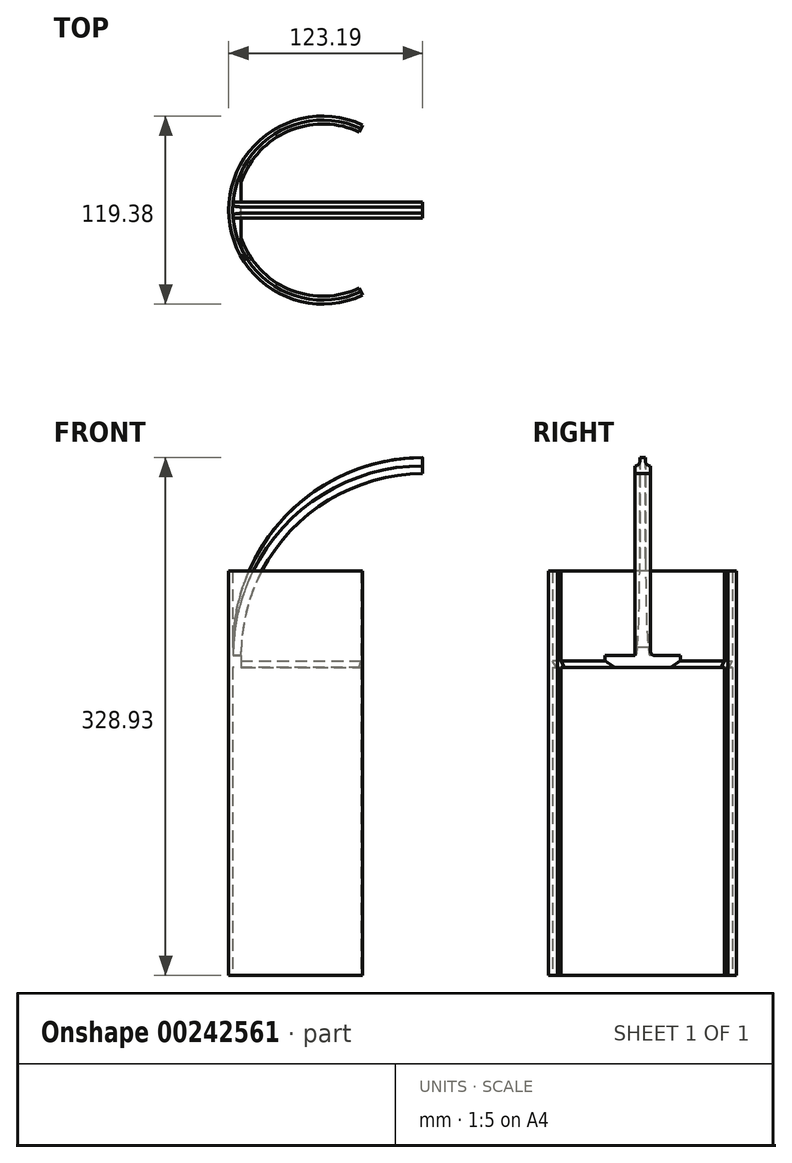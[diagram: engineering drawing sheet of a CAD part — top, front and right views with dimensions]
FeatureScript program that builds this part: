
annotation { "Feature Type Name" : "Feature", "Feature Type Description" : "" }
export const myFeature = defineFeature(function(context is Context, id is Id, definition is map)
    precondition{}
    {
        {
            var Q0;
            Q0=qCreatedBy(makeId("Top.planeOp"),FACE);
            var sketch = newSketch(context, id + "F0", { "sketchPlane" : qUnion([Q0])});
            skLineSegment(sketch, "E0.bottom", {"start": v(0, 5) * mm, "end": v(-31.75, 5) * mm});
            skLineSegment(sketch, "E0.top", {"start": v(0, -5) * mm, "end": v(-31.75, -5) * mm});
            skLineSegment(sketch, "E0.left", {"start": v(0, 5) * mm, "end": v(0, -5) * mm});
            skLineSegment(sketch, "E0.right", {"start": v(-31.75, 5) * mm, "end": v(-31.75, -5) * mm});
            skCircle(sketch, "E1", {"center": v(-63.5, 0) * mm, "radius": 57.15 * mm});
            skLineSegment(sketch, "E2", {"start": v(-63.5, 0) * mm, "end": v(-39.35, 51.8) * mm});
            skLineSegment(sketch, "E3", {"start": v(-63.5, 0) * mm, "end": v(-39.35, -51.8) * mm});
            skCircle(sketch, "E4", {"center": v(-63.5, 0) * mm, "radius": 49.65 * mm});
            skLineSegment(sketch, "E5.bottom", {"start": v(-120.43, -5) * mm, "end": v(-94.98, -5) * mm});
            skLineSegment(sketch, "E5.top", {"start": v(-120.43, 5) * mm, "end": v(-94.98, 5) * mm});
            skLineSegment(sketch, "E5.left", {"start": v(-120.43, -5) * mm, "end": v(-120.43, 5) * mm});
            skLineSegment(sketch, "E5.right", {"start": v(-94.98, -5) * mm, "end": v(-94.98, 5) * mm});
            skPoint(sketch, "E5.middle", {"position": v(-107.7, 0) * mm});
            skLineSegment(sketch, "E6.bottom", {"start": v(-112.9, -5) * mm, "end": v(-115.44, -5) * mm});
            skLineSegment(sketch, "E6.top", {"start": v(-112.9, 5) * mm, "end": v(-115.44, 5) * mm});
            skLineSegment(sketch, "E6.left", {"start": v(-112.9, -5) * mm, "end": v(-112.9, 5) * mm});
            skLineSegment(sketch, "E6.right", {"start": v(-115.44, -5) * mm, "end": v(-115.44, 5) * mm});
            skLineSegment(sketch, "E7", {"start": v(-115.44, -5) * mm, "end": v(-109.06, -19.72) * mm});
            skLineSegment(sketch, "E8", {"start": v(-115.44, 5) * mm, "end": v(-109.06, 19.72) * mm});
            skSolve(sketch);
        }
        {
            var Q0;
            {var subQ0=sQuery(id+"F0.wireOp",EDGE,"E5.left");Q0=makeQuery(id+"F0.imprint","IMPRINT",FACE,{"disambiguationData":[TD([[makeQuery(id+"F0.imprint","IMPRINT",EDGE,{"derivedFrom":subQ0}),1.0]])]});}
            var Q1;
            {var subQ0=sQuery(id+"F0.wireOp",EDGE,"E2");var subQ1=sQuery(id+"F0.wireOp",EDGE,"E1");var subQ2=makeQuery(id+"F0.imprint","INTERSECT",VERTEX,{"derivedFrom":[subQ1,subQ0]});Q1=makeQuery(id+"F0.imprint","IMPRINT",FACE,{"disambiguationData":[TD([[makeQuery(id+"F0.imprint","IMPRINT",EDGE,{"disambiguationData":[TD([[subQ2,1.0]])],"derivedFrom":subQ0}),1.0]])]});}
            var Q2;
            {var subQ0=sQuery(id+"F0.wireOp",EDGE,"E3");var subQ1=sQuery(id+"F0.wireOp",EDGE,"E1");var subQ2=makeQuery(id+"F0.imprint","INTERSECT",VERTEX,{"derivedFrom":[subQ1,subQ0]});Q2=makeQuery(id+"F0.imprint","IMPRINT",FACE,{"disambiguationData":[TD([[makeQuery(id+"F0.imprint","IMPRINT",EDGE,{"disambiguationData":[TD([[subQ2,1.0]])],"derivedFrom":subQ0}),-1.0]])]});}
            var Q3;
            {var subQ5=sQuery(id+"F0.wireOp",EDGE,"E5.left");Q3=makeQuery(id+"F0.imprint","IMPRINT",FACE,{"disambiguationData":[TD([[makeQuery(id+"F0.imprint","IMPRINT",EDGE,{"derivedFrom":subQ5}),-1.0]])]});}
            extrude(context, id + "F1", {"entities" : qUnion([Q0, Q1, Q2, Q3]), "oppositeDirection" : true, "depth" : 7.62 * mm});
        }
        {
            var Q0;
            {var subQ5=sQuery(id+"F0.wireOp",EDGE,"E5.left");Q0=makeQuery(id+"F0.imprint","IMPRINT",FACE,{"disambiguationData":[TD([[makeQuery(id+"F0.imprint","IMPRINT",EDGE,{"derivedFrom":subQ5}),-1.0]])]});}
            var Q1;
            {var subQ0=sQuery(id+"F0.wireOp",EDGE,"E5.left");Q1=makeQuery(id+"F0.imprint","IMPRINT",FACE,{"disambiguationData":[TD([[makeQuery(id+"F0.imprint","IMPRINT",EDGE,{"derivedFrom":subQ0}),1.0]])]});}
            var Q2;
            Q2=sQuery(id+"F0.wireOp",EDGE,"E0.left");
            revolve(context, id + "F2", {"operationType" : NewBodyOperationType.ADD, "entities" : qUnion([Q0, Q1]), "axis" : qUnion([Q2]), "revolveType" : RevolveType.ONE_DIRECTION, "oppositeDirection" : true, "angle" : 90 * degree});
        }
        {
            var Q0;
            Q0=makeQuery(id+"F1.opExtrude","CAP_EDGE",EDGE,{"disambiguationData":[OSD([sQuery(id+"F0.wireOp",EDGE,"E4")])],"isStart":false});
            chamfer(context, id + "F3", {"entities" : qUnion([Q0]), "chamferType" : ChamferType.OFFSET_ANGLE, "width" : 5.08 * mm, "oppositeDirection" : false, "angle" : 61 * degree, "tangentPropagation" : true});
        }
        {
            var Q0;
            Q0=qCreatedBy(makeId("Top.planeOp"),FACE);
            var sketch = newSketch(context, id + "F4", { "sketchPlane" : qUnion([Q0])});
            skArc(sketch, "E9.0", {"start": v(-122.96, -5.22) * mm, "mid": v(-93.34, -51.7) * mm, "end": v(-38.27, -54.1) * mm});
            skArc(sketch, "E9.1", {"start": v(-122.96, 5.22) * mm, "mid": v(-123.2, 0) * mm, "end": v(-122.96, -5.22) * mm});
            skArc(sketch, "E9.2", {"start": v(-38.27, 54.1) * mm, "mid": v(-93.34, 51.7) * mm, "end": v(-122.96, 5.22) * mm});
            skArc(sketch, "E10.0", {"start": v(-39.35, 51.8) * mm, "mid": v(-92.07, 49.5) * mm, "end": v(-120.43, 5) * mm});
            skArc(sketch, "E11.0", {"start": v(-120.43, 5) * mm, "mid": v(-120.65, 0) * mm, "end": v(-120.43, -5) * mm});
            skArc(sketch, "E12.0", {"start": v(-120.43, -5) * mm, "mid": v(-92.07, -49.5) * mm, "end": v(-39.35, -51.8) * mm});
            skLineSegment(sketch, "E13", {"start": v(-39.35, 51.8) * mm, "end": v(-38.27, 54.1) * mm});
            skLineSegment(sketch, "E14", {"start": v(-39.35, -51.8) * mm, "end": v(-38.27, -54.1) * mm});
            skSolve(sketch);
        }
        {
            var Q0;
            Q0 = qSketchRegion(id + "F4", true);
            extrude(context, id + "F5", {"entities" : qUnion([Q0]), "depth" : 53.6 * mm});
        }
        {
            var Q0;
            Q0=makeQuery(id+"F5.opExtrude","CAP_FACE",FACE,{"disambiguationData":[OSD([sQuery(id+"F4.wireOp",EDGE,"E9.0"),sQuery(id+"F4.wireOp",EDGE,"E9.1"),sQuery(id+"F4.wireOp",EDGE,"E9.2"),sQuery(id+"F4.wireOp",EDGE,"E10.0"),sQuery(id+"F4.wireOp",EDGE,"E11.0"),sQuery(id+"F4.wireOp",EDGE,"E12.0"),sQuery(id+"F4.wireOp",EDGE,"E13"),sQuery(id+"F4.wireOp",EDGE,"E14")])],"isStart":true});
            extrude(context, id + "F6", {"entities" : qUnion([Q0]), "operationType" : NewBodyOperationType.ADD, "depth" : 203.2 * mm});
        }
        {
            var Q0;
            {var subQ0=sQuery(id+"F0.wireOp",EDGE,"E6.right");var subQ1=sQuery(id+"F0.wireOp",EDGE,"E2");var subQ2=sQuery(id+"F0.wireOp",EDGE,"E8");var subQ3=sQuery(id+"F0.wireOp",EDGE,"E4");var subQ4=makeQuery(id+"F0.imprint","IMPRINT",EDGE,{"disambiguationData":[TD([[makeQuery(id+"F0.imprint","INTERSECT",VERTEX,{"derivedFrom":[subQ3,subQ2]}),1.0]])],"derivedFrom":subQ3});var subQ5=sQuery(id+"F0.wireOp",EDGE,"E1");Q0=makeQuery(id+"F3.opChamfer","BLEND_EDGE",EDGE,{"blendedFrom":[makeQuery(id+"F1.opExtrude","CAP_EDGE",EDGE,{"disambiguationData":[OSD([subQ3]),TDD([subQ4])],"isStart":false}),makeQuery(id+"F2.boolean.opBoolean","SPLIT",FACE,{"disambiguationData":[TD([makeQuery(id+"F1.opExtrude","SWEPT_FACE",FACE,{"disambiguationData":[OSD([subQ1])]})])],"derivedFrom":makeQuery(id+"F1.opExtrude","CAP_FACE",FACE,{"disambiguationData":[OSD([subQ5,subQ1,sQuery(id+"F0.wireOp",EDGE,"E3"),subQ3,subQ0,sQuery(id+"F0.wireOp",EDGE,"E7"),subQ2])],"isStart":true})})],"blendedInto":[makeQuery(id+"F2.boolean.opBoolean","SPLIT",FACE,{"disambiguationData":[TD([makeQuery(id+"F1.opExtrude","SWEPT_FACE",FACE,{"disambiguationData":[OSD([subQ1])]})])],"derivedFrom":makeQuery(id+"F1.opExtrude","CAP_FACE",FACE,{"disambiguationData":[OSD([subQ5,subQ1,sQuery(id+"F0.wireOp",EDGE,"E3"),subQ3,subQ0,sQuery(id+"F0.wireOp",EDGE,"E7"),subQ2])],"isStart":true})})]});}
            var Q1;
            {var subQ0=sQuery(id+"F0.wireOp",EDGE,"E6.right");var subQ1=sQuery(id+"F0.wireOp",EDGE,"E7");var subQ2=sQuery(id+"F0.wireOp",EDGE,"E4");var subQ3=sQuery(id+"F0.wireOp",EDGE,"E3");var subQ4=makeQuery(id+"F0.imprint","IMPRINT",EDGE,{"disambiguationData":[TD([[makeQuery(id+"F0.imprint","INTERSECT",VERTEX,{"derivedFrom":[subQ2,subQ1]}),-1.0]])],"derivedFrom":subQ2});var subQ5=sQuery(id+"F0.wireOp",EDGE,"E1");Q1=makeQuery(id+"F3.opChamfer","BLEND_EDGE",EDGE,{"blendedFrom":[makeQuery(id+"F1.opExtrude","CAP_EDGE",EDGE,{"disambiguationData":[OSD([subQ2]),TDD([subQ4])],"isStart":false}),makeQuery(id+"F2.boolean.opBoolean","SPLIT",FACE,{"disambiguationData":[TD([makeQuery(id+"F1.opExtrude","SWEPT_FACE",FACE,{"disambiguationData":[OSD([subQ3])]})])],"derivedFrom":makeQuery(id+"F1.opExtrude","CAP_FACE",FACE,{"disambiguationData":[OSD([subQ5,sQuery(id+"F0.wireOp",EDGE,"E2"),subQ3,subQ2,subQ0,subQ1,sQuery(id+"F0.wireOp",EDGE,"E8")])],"isStart":true})})],"blendedInto":[makeQuery(id+"F2.boolean.opBoolean","SPLIT",FACE,{"disambiguationData":[TD([makeQuery(id+"F1.opExtrude","SWEPT_FACE",FACE,{"disambiguationData":[OSD([subQ3])]})])],"derivedFrom":makeQuery(id+"F1.opExtrude","CAP_FACE",FACE,{"disambiguationData":[OSD([subQ5,sQuery(id+"F0.wireOp",EDGE,"E2"),subQ3,subQ2,subQ0,subQ1,sQuery(id+"F0.wireOp",EDGE,"E8")])],"isStart":true})})]});}
            var Q2;
            {var subQ0=sQuery(id+"F0.wireOp",EDGE,"E6.right");var subQ1=sQuery(id+"F0.wireOp",EDGE,"E7");var subQ2=sQuery(id+"F0.wireOp",EDGE,"E4");var subQ3=sQuery(id+"F0.wireOp",EDGE,"E3");var subQ4=sQuery(id+"F0.wireOp",EDGE,"E1");Q2=makeQuery(id+"F3.opChamfer","BLEND_EDGE",EDGE,{"blendedFrom":[makeQuery(id+"F1.opExtrude","CAP_EDGE",EDGE,{"disambiguationData":[OSD([subQ1])],"isStart":false}),makeQuery(id+"F2.boolean.opBoolean","SPLIT",FACE,{"disambiguationData":[TD([makeQuery(id+"F1.opExtrude","SWEPT_FACE",FACE,{"disambiguationData":[OSD([subQ3])]})])],"derivedFrom":makeQuery(id+"F1.opExtrude","CAP_FACE",FACE,{"disambiguationData":[OSD([subQ4,sQuery(id+"F0.wireOp",EDGE,"E2"),subQ3,subQ2,subQ0,subQ1,sQuery(id+"F0.wireOp",EDGE,"E8")])],"isStart":true})})],"blendedInto":[makeQuery(id+"F2.boolean.opBoolean","SPLIT",FACE,{"disambiguationData":[TD([makeQuery(id+"F1.opExtrude","SWEPT_FACE",FACE,{"disambiguationData":[OSD([subQ3])]})])],"derivedFrom":makeQuery(id+"F1.opExtrude","CAP_FACE",FACE,{"disambiguationData":[OSD([subQ4,sQuery(id+"F0.wireOp",EDGE,"E2"),subQ3,subQ2,subQ0,subQ1,sQuery(id+"F0.wireOp",EDGE,"E8")])],"isStart":true})})]});}
            var Q3;
            {var subQ0=sQuery(id+"F0.wireOp",EDGE,"E6.right");var subQ1=sQuery(id+"F0.wireOp",EDGE,"E2");var subQ2=sQuery(id+"F0.wireOp",EDGE,"E8");var subQ3=sQuery(id+"F0.wireOp",EDGE,"E4");var subQ4=sQuery(id+"F0.wireOp",EDGE,"E1");Q3=makeQuery(id+"F3.opChamfer","BLEND_EDGE",EDGE,{"blendedFrom":[makeQuery(id+"F1.opExtrude","CAP_EDGE",EDGE,{"disambiguationData":[OSD([subQ2])],"isStart":false}),makeQuery(id+"F2.boolean.opBoolean","SPLIT",FACE,{"disambiguationData":[TD([makeQuery(id+"F1.opExtrude","SWEPT_FACE",FACE,{"disambiguationData":[OSD([subQ1])]})])],"derivedFrom":makeQuery(id+"F1.opExtrude","CAP_FACE",FACE,{"disambiguationData":[OSD([subQ4,subQ1,sQuery(id+"F0.wireOp",EDGE,"E3"),subQ3,subQ0,sQuery(id+"F0.wireOp",EDGE,"E7"),subQ2])],"isStart":true})})],"blendedInto":[makeQuery(id+"F2.boolean.opBoolean","SPLIT",FACE,{"disambiguationData":[TD([makeQuery(id+"F1.opExtrude","SWEPT_FACE",FACE,{"disambiguationData":[OSD([subQ1])]})])],"derivedFrom":makeQuery(id+"F1.opExtrude","CAP_FACE",FACE,{"disambiguationData":[OSD([subQ4,subQ1,sQuery(id+"F0.wireOp",EDGE,"E3"),subQ3,subQ0,sQuery(id+"F0.wireOp",EDGE,"E7"),subQ2])],"isStart":true})})]});}
            chamfer(context, id + "F7", {"entities" : qUnion([Q0, Q1, Q2, Q3]), "width" : 5.08 * mm, "tangentPropagation" : true});
        }
        {
            var Q0;
            Q0=qCreatedBy(makeId("Top.planeOp"),FACE);
            var sketch = newSketch(context, id + "F8", { "sketchPlane" : qUnion([Q0])});
            skLineSegment(sketch, "E15.bottom", {"start": v(-120.62, -1.86) * mm, "end": v(-115.44, -1.86) * mm});
            skLineSegment(sketch, "E15.top", {"start": v(-120.62, 1.86) * mm, "end": v(-115.44, 1.86) * mm});
            skLineSegment(sketch, "E15.left", {"start": v(-120.62, -1.86) * mm, "end": v(-120.62, 1.86) * mm});
            skLineSegment(sketch, "E15.right", {"start": v(-115.44, -1.86) * mm, "end": v(-115.44, 1.86) * mm});
            skPoint(sketch, "E15.middle", {"position": v(-118.03, 0) * mm});
            skCircle(sketch, "E16.0", {"center": v(-63.5, 0) * mm, "radius": 57.15 * mm});
            skCircle(sketch, "E17.0", {"center": v(-63.5, 0) * mm, "radius": 49.65 * mm});
            skLineSegment(sketch, "E18.0", {"start": v(-115.44, -5) * mm, "end": v(-115.44, 5) * mm});
            skSolve(sketch);
        }
        {
            var Q0;
            {var subQ0=sQuery(id+"F8.wireOp",EDGE,"E15.bottom");Q0=makeQuery(id+"F8.imprint","IMPRINT",FACE,{"disambiguationData":[TD([[makeQuery(id+"F8.imprint","IMPRINT",EDGE,{"derivedFrom":subQ0}),1.0]])]});}
            var Q1;
            {var subQ0=sQuery(id+"F8.wireOp",EDGE,"E15.left");Q1=makeQuery(id+"F8.imprint","IMPRINT",FACE,{"disambiguationData":[TD([[makeQuery(id+"F8.imprint","IMPRINT",EDGE,{"derivedFrom":subQ0}),1.0]])]});}
            var Q2;
            Q2=sQuery(id+"F0.wireOp",EDGE,"E0.left");
            revolve(context, id + "F9", {"entities" : qUnion([Q0, Q1]), "axis" : qUnion([Q2]), "revolveType" : RevolveType.ONE_DIRECTION, "oppositeDirection" : true, "angle" : 90 * degree});
        }
        {
            var Q0;
            Q0=makeQuery(id+"F9.opRevolve","SWEPT_BODY",BODY,{"disambiguationData":[OSD([sQuery(id+"F8.wireOp",EDGE,"E15.bottom"),sQuery(id+"F8.wireOp",EDGE,"E15.top"),sQuery(id+"F8.wireOp",EDGE,"E16.0"),sQuery(id+"F8.wireOp",EDGE,"E18.0")])]});
            var Q1;
            {var subQ0=sQuery(id+"F4.wireOp",EDGE,"E14");var subQ1=sQuery(id+"F4.wireOp",EDGE,"E9.0");Q1=makeQuery(id+"F6.boolean.opBoolean","MERGE",EDGE,{"derivedFrom":[makeQuery(id+"F5.opExtrude","SWEPT_EDGE",EDGE,{"disambiguationData":[OSD([subQ1,subQ0])]}),makeQuery(id+"F6.opExtrude","SWEPT_EDGE",EDGE,{"disambiguationData":[OSD([subQ1,subQ0])]})]});}
            transform(context, id + "F10", {"entities" : qUnion([Q0]), "transformType" : TransformType.TRANSLATION_3D, "dx" : 0 * mm, "dy" : 0 * mm, "dz" : 5.08 * mm, "makeCopy" : false});
        }
        {
            var Q0;
            Q0=makeQuery(id+"F9.opRevolve","CAP_FACE",FACE,{"disambiguationData":[OSD([sQuery(id+"F8.wireOp",EDGE,"E15.bottom"),sQuery(id+"F8.wireOp",EDGE,"E15.top"),sQuery(id+"F8.wireOp",EDGE,"E16.0"),sQuery(id+"F8.wireOp",EDGE,"E18.0")])],"isStart":true});
            extrude(context, id + "F11", {"entities" : qUnion([Q0]), "operationType" : NewBodyOperationType.ADD, "depth" : 10.26 * mm});
        }
        {
            var Q0;
            Q0=makeQuery(id+"F2.opRevolve","CAP_EDGE",EDGE,{"disambiguationData":[OSD([sQuery(id+"F0.wireOp",EDGE,"E5.top")])],"isStart":true});
            var Q1;
            Q1=makeQuery(id+"F2.opRevolve","CAP_EDGE",EDGE,{"disambiguationData":[OSD([sQuery(id+"F0.wireOp",EDGE,"E5.bottom")])],"isStart":true});
            var Q2;
            Q2=makeQuery(id+"F11.boolean.opBoolean","INTERSECT",EDGE,{"derivedFrom":[makeQuery(id+"F2.opRevolve","SWEPT_FACE",FACE,{"disambiguationData":[OSD([sQuery(id+"F0.wireOp",EDGE,"E1")])]}),makeQuery(id+"F11.opExtrude","SWEPT_FACE",FACE,{"disambiguationData":[OSD([sQuery(id+"F8.wireOp",EDGE,"E15.bottom")])]})]});
            var Q3;
            Q3=makeQuery(id+"F11.boolean.opBoolean","INTERSECT",EDGE,{"derivedFrom":[makeQuery(id+"F2.opRevolve","SWEPT_FACE",FACE,{"disambiguationData":[OSD([sQuery(id+"F0.wireOp",EDGE,"E1")])]}),makeQuery(id+"F11.opExtrude","SWEPT_FACE",FACE,{"disambiguationData":[OSD([sQuery(id+"F8.wireOp",EDGE,"E15.top")])]})]});
            fillet(context, id + "F12", {"entities" : qUnion([Q0, Q1, Q2, Q3]), "radius" : 2.6 * mm, "tangentPropagation" : true, "allowEdgeOverflow" : false});
        }
    });
